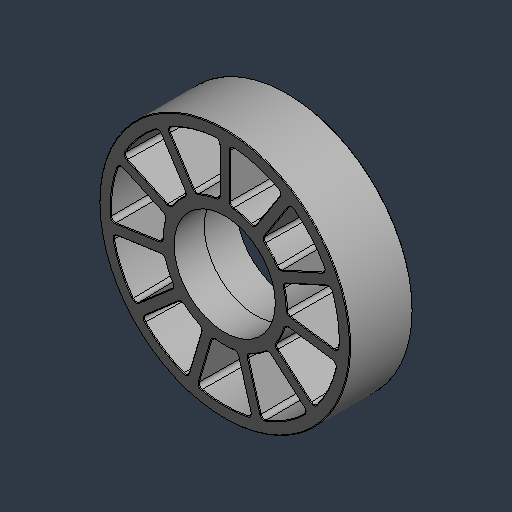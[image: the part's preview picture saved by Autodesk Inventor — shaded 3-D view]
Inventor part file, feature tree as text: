
AUTODESK INVENTOR PART (.ipt)
format: ipt  version: 2024.3 (Build 283343000, 343)  size: 844,288 bytes
history: native  units: mm (DEFAULTED — no unit token found)
features: fillet x1
ambient origin geometry x8: Origin, YZ Plane, XZ Plane, XY Plane, X Axis, Y Axis, Z Axis, Center Point
bodies: Solid1 (feature_tree)
feature tree (1):
  fillet  "Fillet2"  [1 undecoded]
note: 1 required parameter value undecoded (feature->parameter linkage not recoverable at this tier; creation-order binding heuristic only, values carry confidence <= 0.55)
